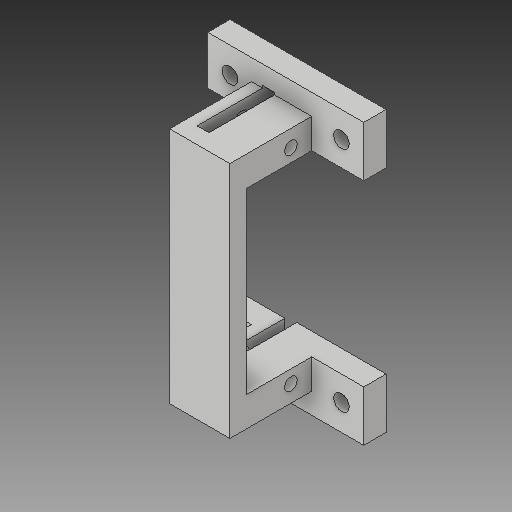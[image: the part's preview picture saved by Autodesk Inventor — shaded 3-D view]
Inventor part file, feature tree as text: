
AUTODESK INVENTOR PART (.ipt)
format: ipt  version: 2018 (Build 220112000, 112)  size: 265,216 bytes
history: native  units: mm
features: reference x19, extrude x11, sketch x11, other x7, projected_geometry x3
ambient origin geometry x8: Origin, YZ Plane, XZ Plane, XY Plane, X Axis, Y Axis, Z Axis, Center Point
bodies: Body1 (feature_tree)
feature tree (51):
  other  "ソリッド1"
  extrude  "押し出し1"  Depth=12.0mm
  extrude  "押し出し2"  Depth=14.0mm TaperAngle=0.0deg
  extrude  "押し出し3"  Depth=1.7mm
  extrude  "押し出し4"  Depth=14.0mm TaperAngle=0.0deg
  extrude  "押し出し5"  Depth=0.2mm
  extrude  "押し出し6"  Depth=0.2mm
  extrude  "押し出し7"  Depth=0.2mm
  extrude  "押し出し8"  Depth=0.2mm
  extrude  "押し出し9"  Depth=14.0mm TaperAngle=0.0deg
  extrude  "押し出し10"  Depth=7.0mm
  extrude  "押し出し11"  Depth=3.0mm
  sketch  "スケッチ1"
  reference  "参照1"
  reference  "参照2"
  reference  "参照3"
  reference  "参照4"
  reference  "参照5"
  reference  "参照6"
  reference  "参照7"
  sketch  "スケッチ2"
  reference  "参照8"
  reference  "参照9"
  sketch  "スケッチ3"
  reference  "参照10"
  reference  "参照11"
  reference  "参照12"
  reference  "参照13"
  reference  "参照14"
  sketch  "スケッチ4"
  sketch  "スケッチ5"
  sketch  "スケッチ6"
  sketch  "スケッチ7"
  reference  "参照15"
  reference  "参照16"
  reference  "参照17"
  reference  "参照18"
  sketch  "スケッチ8"
  sketch  "スケッチ9"
  projected_geometry  "投影ループ1"
  projected_geometry  "投影ループ2"
  projected_geometry  "投影ループ3"
  sketch  "スケッチ10"
  reference  "参照19"
  sketch  "スケッチ11"
  parser-record x1  (decoder bookkeeping rows leaked as tree rows — omitted from the tree; the rows remain in map.json)
  other  "M-R-H.iam"
  other  "R-H-02 v1:1"
  other  "ASV-15MG:1"
  other  "R-T v4:1"
  other  "R-T-06 v1:1"
note: 1 file-system path scrubbed to <path> (originals preserved in map.json)
